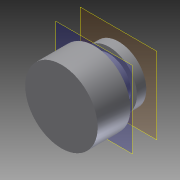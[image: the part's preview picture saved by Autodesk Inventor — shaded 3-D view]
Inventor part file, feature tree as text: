
AUTODESK INVENTOR PART (.ipt)
format: ipt  version: 2012 (Build 160160000, 160)  size: 95,744 bytes
history: native  units: in
note: dims shown in document units (in); Inventor stores cm internally (conversion verified against a paired STEP export)
features: extrude x3, sketch x3, plane x2
ambient origin geometry x8: Origin, YZ Plane, XZ Plane, XY Plane, X Axis, Y Axis, Z Axis, Center Point
bodies: Solid1 (feature_tree)
feature tree (8):
  plane  "Work Plane3"
  plane  "Work Plane4"
  extrude  "Extrusion5"  Depth=0.6264in
  extrude  "Extrusion6"  Depth=0.4921in
  extrude  "Extrusion7"  Depth=0.8183in
  sketch  "Sketch7"  dims[d17=0.2756in d18=0.6264in]
  sketch  "Sketch8"  dims[d19=0.1063in d20=0.0in d21=0.4921in]
  sketch  "Sketch9"  dims[d22=0.1063in d23=0.0in d24=0.8183in d25=0.3701in d26=0.0in]
